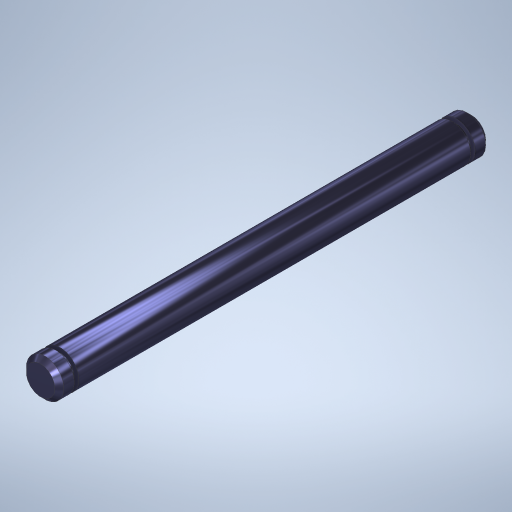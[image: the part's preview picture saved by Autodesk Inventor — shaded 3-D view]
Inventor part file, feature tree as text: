
AUTODESK INVENTOR PART (.ipt)
format: ipt  version: 2023.1 (Build 271208000, 208)  size: 297,984 bytes
history: native  units: in
note: dims shown in document units (in); Inventor stores cm internally (conversion verified against a paired STEP export)
features: extrude x3, sketch x3, chamfer x1, mirror x1
ambient origin geometry x8: Origin, YZ Plane, XZ Plane, XY Plane, X Axis, Y Axis, Z Axis, Center Point
bodies: Solid1 (feature_tree)
feature tree (8):
  extrude  "Extrusion1"  Depth=1.2998in TaperAngle=0.0deg
  extrude  "Extrusion2"  Depth=0.015in TaperAngle=0.0deg
  extrude  "Extrusion3"  Depth=0.015in TaperAngle=45.0deg
  chamfer  "Chamfer1"  [1 undecoded]
  mirror  "Mirror1"
  sketch  "Sketch1"  dims[d0=0.125in d1=1.2998in d2=0.0in]
  sketch  "Sketch2"  dims[d3=0.0938in d4=0.015in d5=0.0in]
  sketch  "Sketch3"  dims[d6=0.05in d7=0.0in d8=0.015in d9=0.125in d10=45.0deg]
note: 1 required parameter value undecoded (feature->parameter linkage not recoverable at this tier; creation-order binding heuristic only, values carry confidence <= 0.55)
